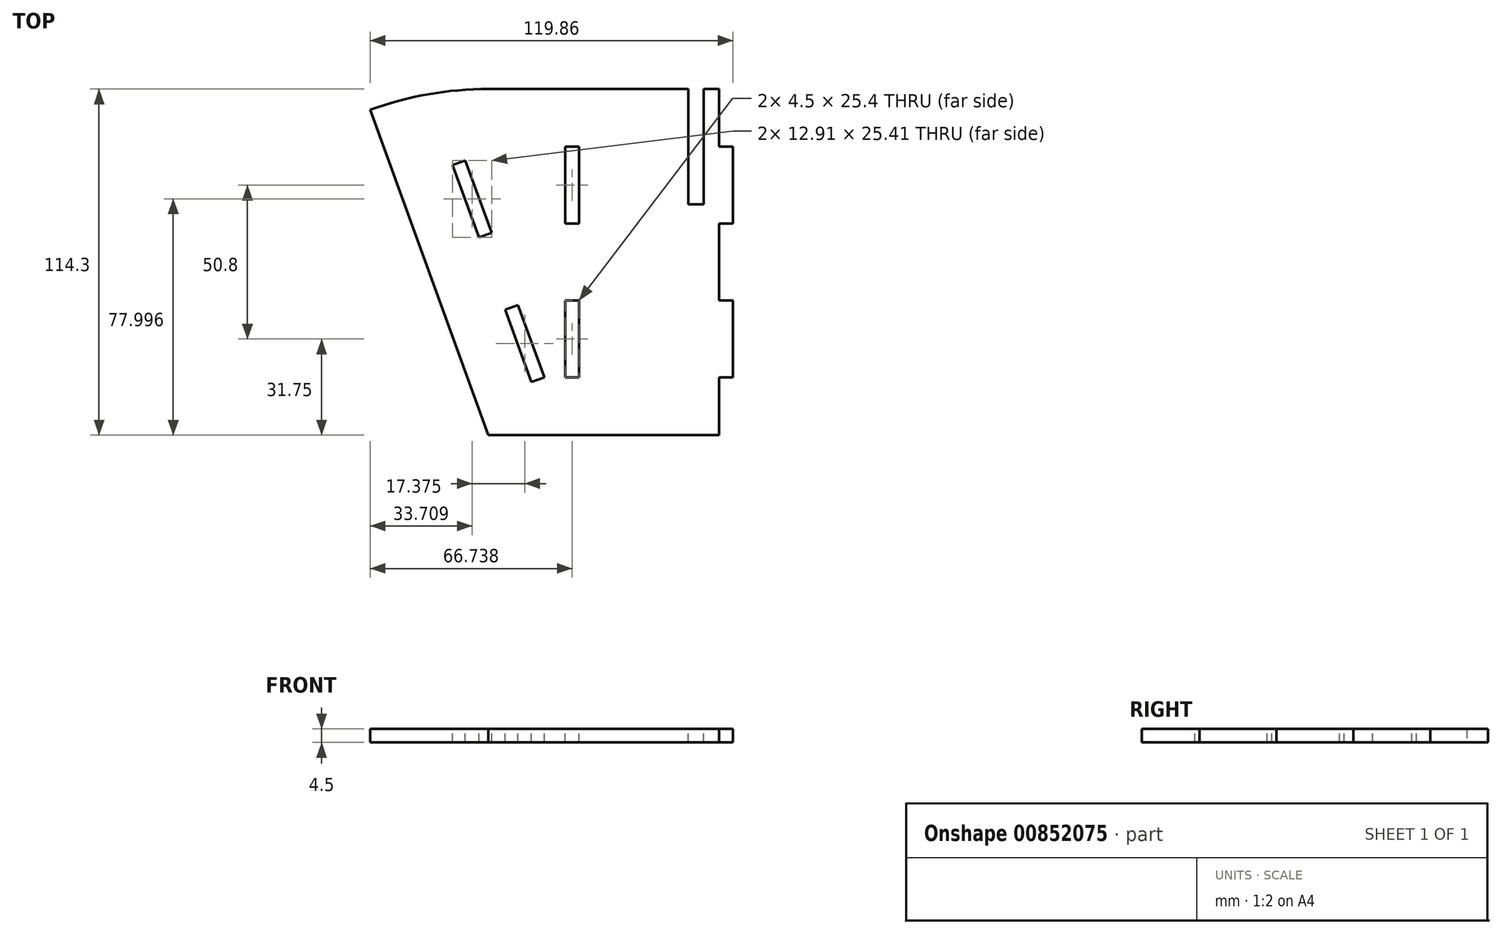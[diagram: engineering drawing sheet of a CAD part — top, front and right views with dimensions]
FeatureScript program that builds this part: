
annotation { "Feature Type Name" : "Feature", "Feature Type Description" : "" }
export const myFeature = defineFeature(function(context is Context, id is Id, definition is map)
    precondition{}
    {
        {
            var Q0;
            Q0=qCreatedBy(makeId("Top.planeOp"),FACE);
            var sketch = newSketch(context, id + "F0", { "sketchPlane" : qUnion([Q0])});
            skLineSegment(sketch, "E0.bottom", {"start": v(-38.1, 57.15) * mm, "end": v(38.1, 57.15) * mm});
            skLineSegment(sketch, "E0.top", {"start": v(-38.1, -57.15) * mm, "end": v(38.1, -57.15) * mm});
            skLineSegment(sketch, "E0.left", {"start": v(-38.1, 57.15) * mm, "end": v(-38.1, 38.1) * mm, "construction": true});
            skLineSegment(sketch, "E1", {"start": v(-38.1, 57.15) * mm, "end": v(38.1, -57.15) * mm, "construction": true});
            skLineSegment(sketch, "E2", {"start": v(-38.1, 38.1) * mm, "end": v(-42.67, 38.1) * mm, "construction": true});
            skLineSegment(sketch, "E3", {"start": v(-42.67, 38.1) * mm, "end": v(-42.67, 12.7) * mm, "construction": true});
            skLineSegment(sketch, "E4", {"start": v(-42.67, 12.7) * mm, "end": v(-38.1, 12.7) * mm, "construction": true});
            skLineSegment(sketch, "E5", {"start": v(-38.1, 12.7) * mm, "end": v(-38.1, 0) * mm, "construction": true});
            skLineSegment(sketch, "E6", {"start": v(-38.1, 0) * mm, "end": v(38.1, 0) * mm, "construction": true});
            skPoint(sketch, "E7.start.orphan", {"position": v(38.1, 0) * mm});
            skLineSegment(sketch, "E8", {"start": v(38.1, 57.15) * mm, "end": v(-38.1, -57.15) * mm, "construction": true});
            skLineSegment(sketch, "E9", {"start": v(38.1, 57.15) * mm, "end": v(38.1, -57.15) * mm, "construction": true});
            skLineSegment(sketch, "E10.MirrorCS", {"start": v(-42.67, -12.7) * mm, "end": v(-38.1, -12.7) * mm, "construction": true});
            skLineSegment(sketch, "E11.MirrorCS", {"start": v(-38.1, -38.1) * mm, "end": v(-42.67, -38.1) * mm, "construction": true});
            skLineSegment(sketch, "E12.MirrorCS", {"start": v(-38.1, -12.7) * mm, "end": v(-38.1, 0) * mm, "construction": true});
            skLineSegment(sketch, "E13.MirrorCS", {"start": v(-38.1, -57.15) * mm, "end": v(-38.1, -38.1) * mm, "construction": true});
            skLineSegment(sketch, "E14.MirrorCS", {"start": v(-42.67, -38.1) * mm, "end": v(-42.67, -12.7) * mm, "construction": true});
            skLineSegment(sketch, "E15.MirrorCS", {"start": v(38.1, -38.1) * mm, "end": v(42.67, -38.1) * mm});
            skLineSegment(sketch, "E16.MirrorCS", {"start": v(42.67, -12.7) * mm, "end": v(38.1, -12.7) * mm});
            skLineSegment(sketch, "E17.MirrorCS", {"start": v(38.1, 38.1) * mm, "end": v(42.67, 38.1) * mm});
            skLineSegment(sketch, "E18.MirrorCS", {"start": v(42.67, 12.7) * mm, "end": v(38.1, 12.7) * mm});
            skLineSegment(sketch, "E19.MirrorCS", {"start": v(42.67, 38.1) * mm, "end": v(42.67, 12.7) * mm});
            skLineSegment(sketch, "E20.MirrorCS", {"start": v(38.1, -57.15) * mm, "end": v(38.1, -38.1) * mm});
            skLineSegment(sketch, "E21.MirrorCS", {"start": v(38.1, 57.15) * mm, "end": v(38.1, 38.1) * mm});
            skLineSegment(sketch, "E22.MirrorCS", {"start": v(38.1, 12.7) * mm, "end": v(38.1, 0) * mm});
            skLineSegment(sketch, "E23.MirrorCS", {"start": v(42.67, -38.1) * mm, "end": v(42.67, -12.7) * mm});
            skLineSegment(sketch, "E24.MirrorCS", {"start": v(38.1, -12.7) * mm, "end": v(38.1, 0) * mm});
            skArc(sketch, "E25", {"start": v(-38.1, 57.15) * mm, "mid": v(-57.95, 55.41) * mm, "end": v(-77.2, 50.26) * mm});
            skLineSegment(sketch, "E26", {"start": v(-38.1, -57.15) * mm, "end": v(-77.2, 50.26) * mm});
            skSolve(sketch);
        }
        {
            var Q0;
            Q0 = qSketchRegion(id + "F0", true);
            extrude(context, id + "F1", {"entities" : qUnion([Q0]), "depth" : 4.5 * mm, "offsetDistance" : 25.4 * mm});
        }
        {
            var Q0;
            Q0=makeQuery(id+"F1.opExtrude","CAP_FACE",FACE,{"disambiguationData":[OSD([sQuery(id+"F0.wireOp",EDGE,"E0.bottom"),sQuery(id+"F0.wireOp",EDGE,"E0.top"),sQuery(id+"F0.wireOp",EDGE,"E0.left"),sQuery(id+"F0.wireOp",EDGE,"E2"),sQuery(id+"F0.wireOp",EDGE,"E3"),sQuery(id+"F0.wireOp",EDGE,"E4"),sQuery(id+"F0.wireOp",EDGE,"E5"),sQuery(id+"F0.wireOp",EDGE,"E10.MirrorCS"),sQuery(id+"F0.wireOp",EDGE,"E11.MirrorCS"),sQuery(id+"F0.wireOp",EDGE,"E12.MirrorCS"),sQuery(id+"F0.wireOp",EDGE,"E13.MirrorCS"),sQuery(id+"F0.wireOp",EDGE,"E14.MirrorCS"),sQuery(id+"F0.wireOp",EDGE,"E15.MirrorCS"),sQuery(id+"F0.wireOp",EDGE,"E16.MirrorCS"),sQuery(id+"F0.wireOp",EDGE,"E17.MirrorCS"),sQuery(id+"F0.wireOp",EDGE,"E18.MirrorCS"),sQuery(id+"F0.wireOp",EDGE,"E19.MirrorCS"),sQuery(id+"F0.wireOp",EDGE,"E20.MirrorCS"),sQuery(id+"F0.wireOp",EDGE,"E21.MirrorCS"),sQuery(id+"F0.wireOp",EDGE,"E22.MirrorCS"),sQuery(id+"F0.wireOp",EDGE,"E23.MirrorCS"),sQuery(id+"F0.wireOp",EDGE,"E24.MirrorCS")])],"isStart":false});
            var sketch = newSketch(context, id + "F2", { "sketchPlane" : qUnion([Q0])});
            skLineSegment(sketch, "E27.bottom", {"start": v(-38.1, 57.15) * mm, "end": v(38.1, 57.15) * mm, "construction": true});
            skLineSegment(sketch, "E27.top", {"start": v(-38.1, -57.15) * mm, "end": v(38.1, -57.15) * mm, "construction": true});
            skLineSegment(sketch, "E27.left", {"start": v(-38.1, 57.15) * mm, "end": v(-38.1, -57.15) * mm, "construction": true});
            skLineSegment(sketch, "E27.right", {"start": v(38.1, 57.15) * mm, "end": v(38.1, -57.15) * mm, "construction": true});
            skLineSegment(sketch, "E28", {"start": v(-12.7, 57.15) * mm, "end": v(-12.7, -57.15) * mm, "construction": true});
            skLineSegment(sketch, "E29.bottom", {"start": v(-12.7, 38.1) * mm, "end": v(-8.2, 38.1) * mm});
            skLineSegment(sketch, "E29.top", {"start": v(-12.7, 12.7) * mm, "end": v(-8.2, 12.7) * mm});
            skLineSegment(sketch, "E29.left", {"start": v(-12.7, 38.1) * mm, "end": v(-12.7, 12.7) * mm});
            skLineSegment(sketch, "E29.right", {"start": v(-8.2, 38.1) * mm, "end": v(-8.2, 12.7) * mm});
            skLineSegment(sketch, "E30", {"start": v(38.1, 38.1) * mm, "end": v(-8.2, 38.1) * mm, "construction": true});
            skLineSegment(sketch, "E31", {"start": v(38.1, 12.7) * mm, "end": v(-8.2, 12.7) * mm, "construction": true});
            skLineSegment(sketch, "E32.MirrorCS", {"start": v(-12.7, -12.7) * mm, "end": v(-8.2, -12.7) * mm});
            skLineSegment(sketch, "E33.MirrorCS", {"start": v(-12.7, -38.1) * mm, "end": v(-8.2, -38.1) * mm});
            skLineSegment(sketch, "E34.MirrorCS", {"start": v(-8.2, -38.1) * mm, "end": v(-8.2, -12.7) * mm});
            skLineSegment(sketch, "E35.MirrorCS", {"start": v(-12.7, -38.1) * mm, "end": v(-12.7, -12.7) * mm});
            skLineSegment(sketch, "E36", {"start": v(-12.7, -57.15) * mm, "end": v(-53.9, 56.05) * mm, "construction": true});
            skLineSegment(sketch, "E37", {"start": v(-45.71, 33.55) * mm, "end": v(-37.02, 9.68) * mm});
            skLineSegment(sketch, "E38", {"start": v(-37.02, 9.68) * mm, "end": v(-41.25, 8.14) * mm});
            skLineSegment(sketch, "E39", {"start": v(-41.25, 8.14) * mm, "end": v(-49.94, 32.01) * mm});
            skLineSegment(sketch, "E40", {"start": v(-49.94, 32.01) * mm, "end": v(-45.71, 33.55) * mm});
            skLineSegment(sketch, "E41", {"start": v(-19.65, -38.06) * mm, "end": v(-28.34, -14.19) * mm});
            skLineSegment(sketch, "E42", {"start": v(-28.34, -14.19) * mm, "end": v(-32.56, -15.72) * mm});
            skLineSegment(sketch, "E43", {"start": v(-32.56, -15.72) * mm, "end": v(-23.87, -39.6) * mm});
            skLineSegment(sketch, "E44", {"start": v(-23.87, -39.6) * mm, "end": v(-19.65, -38.06) * mm});
            skLineSegment(sketch, "E45.bottom", {"start": v(27.94, 57.15) * mm, "end": v(33.02, 57.15) * mm});
            skLineSegment(sketch, "E45.top", {"start": v(27.94, 19.05) * mm, "end": v(33.02, 19.05) * mm});
            skLineSegment(sketch, "E45.left", {"start": v(27.94, 57.15) * mm, "end": v(27.94, 19.05) * mm});
            skLineSegment(sketch, "E45.right", {"start": v(33.02, 57.15) * mm, "end": v(33.02, 19.05) * mm});
            skSolve(sketch);
        }
        {
            var Q0;
            Q0 = qSketchRegion(id + "F2", true);
            extrude(context, id + "F3", {"entities" : qUnion([Q0]), "operationType" : NewBodyOperationType.REMOVE, "endBound" : BoundingType.THROUGH_ALL, "oppositeDirection" : true, "depth" : 25.4 * mm, "offsetDistance" : 25.4 * mm});
        }
    });
